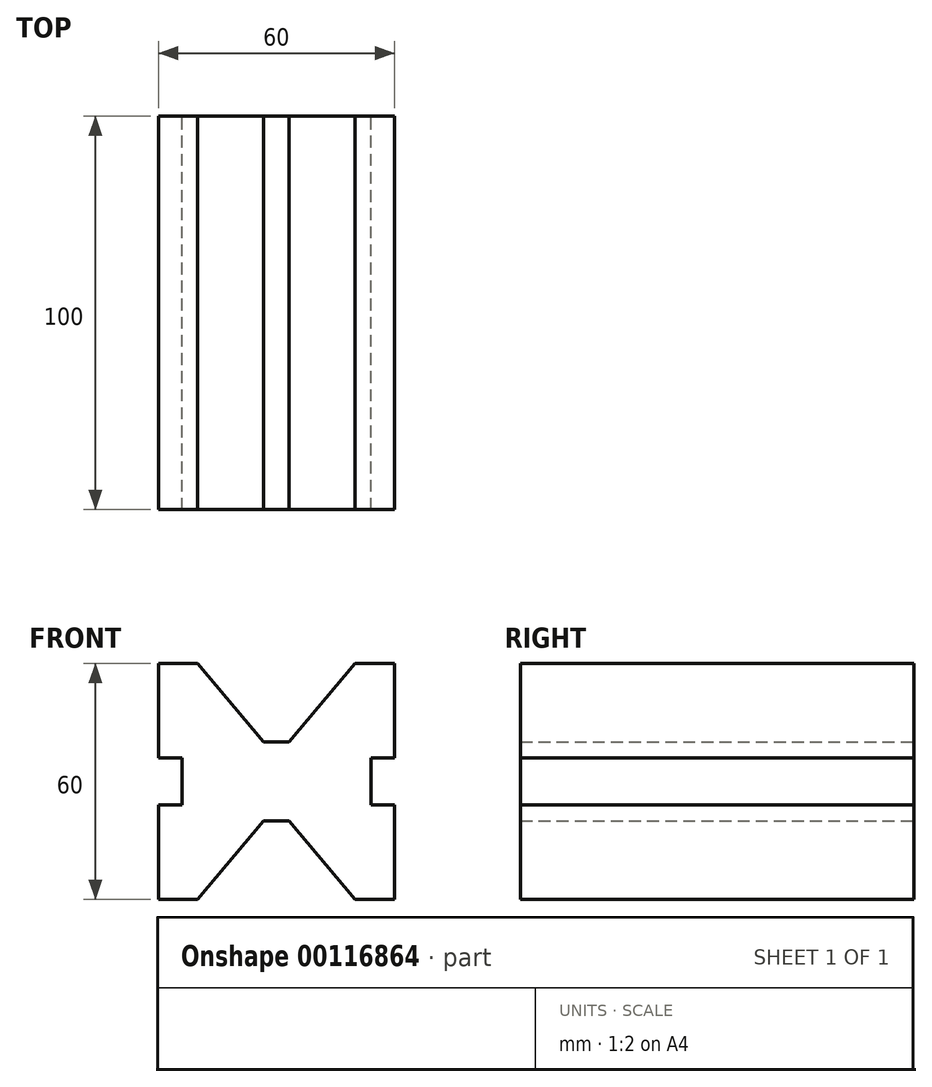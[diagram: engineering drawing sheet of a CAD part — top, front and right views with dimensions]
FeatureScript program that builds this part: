
annotation { "Feature Type Name" : "Feature", "Feature Type Description" : "" }
export const myFeature = defineFeature(function(context is Context, id is Id, definition is map)
    precondition{}
    {
        {
            var Q0;
            Q0=qCreatedBy(makeId("Front.planeOp"),FACE);
            var sketch = newSketch(context, id + "F0", { "sketchPlane" : qUnion([Q0])});
            skLineSegment(sketch, "E0.bottom", {"start": v(0, 0) * mm, "end": v(10, 0) * mm});
            skLineSegment(sketch, "E0.top", {"start": v(0, 60) * mm, "end": v(60, 60) * mm});
            skLineSegment(sketch, "E0.left", {"start": v(0, 0) * mm, "end": v(0, 60) * mm});
            skLineSegment(sketch, "E0.right", {"start": v(60, 0) * mm, "end": v(60, 60) * mm});
            skLineSegment(sketch, "E1.bottom", {"start": v(0, 36) * mm, "end": v(6, 36) * mm});
            skLineSegment(sketch, "E1.top", {"start": v(0, 24) * mm, "end": v(6, 24) * mm});
            skLineSegment(sketch, "E1.left", {"start": v(0, 36) * mm, "end": v(0, 24) * mm});
            skLineSegment(sketch, "E1.right", {"start": v(6, 36) * mm, "end": v(6, 24) * mm});
            skLineSegment(sketch, "E2.bottom", {"start": v(60, 36) * mm, "end": v(54, 36) * mm});
            skLineSegment(sketch, "E2.top", {"start": v(60, 24) * mm, "end": v(54, 24) * mm});
            skLineSegment(sketch, "E2.left", {"start": v(60, 36) * mm, "end": v(60, 24) * mm});
            skLineSegment(sketch, "E2.right", {"start": v(54, 36) * mm, "end": v(54, 24) * mm});
            skLineSegment(sketch, "E3", {"start": v(30, 60) * mm, "end": v(30, 0) * mm, "construction": true});
            skLineSegment(sketch, "E4", {"start": v(0, 30) * mm, "end": v(60, 30) * mm, "construction": true});
            skPoint(sketch, "E4.endSnap0", {"position": v(60, 30) * mm});
            skPoint(sketch, "E4.endSnap1", {"position": v(6, 30) * mm});
            skLineSegment(sketch, "E5", {"start": v(10, 0) * mm, "end": v(26.78, 20) * mm});
            skLineSegment(sketch, "E6", {"start": v(26.78, 20) * mm, "end": v(33.22, 20) * mm});
            skLineSegment(sketch, "E7", {"start": v(33.22, 20) * mm, "end": v(50, 0) * mm});
            skLineSegment(sketch, "E8.MirrorCS", {"start": v(10, 60) * mm, "end": v(26.78, 40) * mm});
            skLineSegment(sketch, "E9.MirrorCS", {"start": v(26.78, 40) * mm, "end": v(33.22, 40) * mm});
            skLineSegment(sketch, "E10.MirrorCS", {"start": v(33.22, 40) * mm, "end": v(50, 60) * mm});
            skLineSegment(sketch, "E11.trimOffspring", {"start": v(50, 0) * mm, "end": v(60, 0) * mm});
            skLineSegment(sketch, "E12", {"start": v(10, 0) * mm, "end": v(50, 0) * mm});
            skSolve(sketch);
        }
        {
            var Q0;
            {var subQ7=sQuery(id+"F0.wireOp",EDGE,"E0.bottom");Q0=makeQuery(id+"F0.imprint","IMPRINT",FACE,{"disambiguationData":[TD([[makeQuery(id+"F0.imprint","IMPRINT",EDGE,{"derivedFrom":subQ7}),1.0]])]});}
            extrude(context, id + "F1", {"entities" : qUnion([Q0]), "depth" : 100 * mm});
        }
    });
